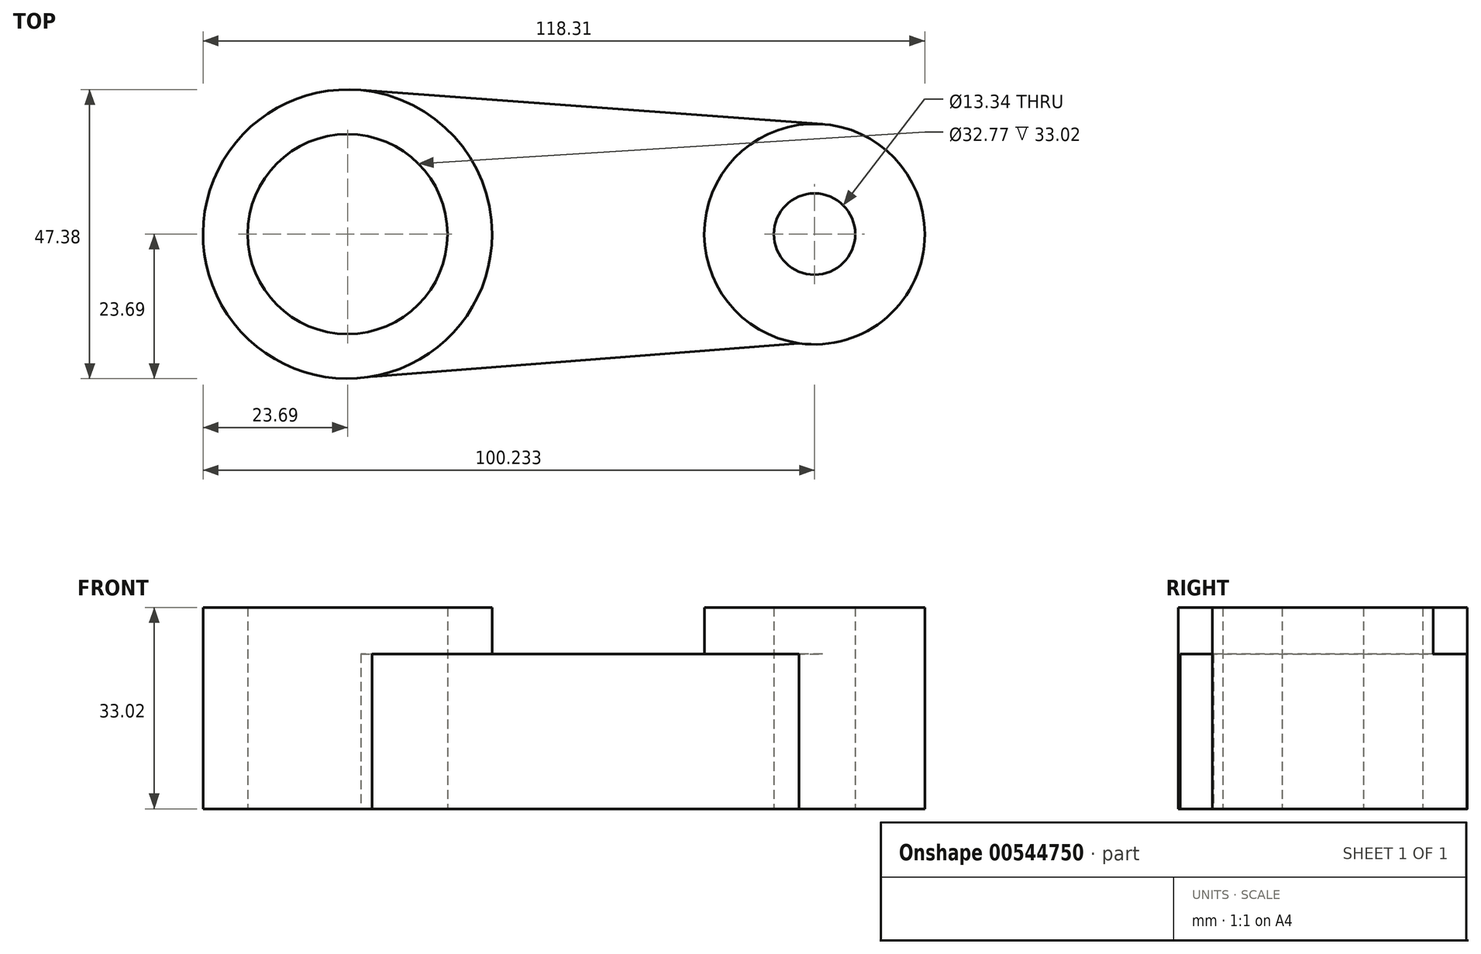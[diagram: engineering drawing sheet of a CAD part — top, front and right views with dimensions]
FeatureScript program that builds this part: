
annotation { "Feature Type Name" : "Feature", "Feature Type Description" : "" }
export const myFeature = defineFeature(function(context is Context, id is Id, definition is map)
    precondition{}
    {
        {
            var Q0;
            Q0=qCreatedBy(makeId("Top.planeOp"),FACE);
            var sketch = newSketch(context, id + "F0", { "sketchPlane" : qUnion([Q0])});
            skCircle(sketch, "E0", {"center": v(0, 0) * mm, "radius": 23.7 * mm});
            skCircle(sketch, "E1", {"center": v(76.54, 0) * mm, "radius": 18.07 * mm});
            skLineSegment(sketch, "E2", {"start": v(2.16, 23.6) * mm, "end": v(77.87, 18.03) * mm});
            skLineSegment(sketch, "E3", {"start": v(4, -23.35) * mm, "end": v(75.29, -17.8) * mm});
            skCircle(sketch, "E4", {"center": v(76.54, 0) * mm, "radius": 6.67 * mm});
            skCircle(sketch, "E5", {"center": v(0, 0) * mm, "radius": 16.38 * mm});
            skSolve(sketch);
        }
        {
            var Q0;
            {var subQ0=sQuery(id+"F0.wireOp",EDGE,"E2");Q0=makeQuery(id+"F0.imprint","IMPRINT",FACE,{"disambiguationData":[TD([[makeQuery(id+"F0.imprint","IMPRINT",EDGE,{"derivedFrom":subQ0}),-1.0]])]});}
            var Q1;
            Q1=makeQuery(id+"F0.imprint","IMPRINT",FACE,{"disambiguationData":[TD([[makeQuery(id+"F0.imprint","IMPRINT",EDGE,{"derivedFrom":sQuery(id+"F0.wireOp",EDGE,"E4")}),-1.0]])]});
            var Q2;
            Q2=makeQuery(id+"F0.imprint","IMPRINT",FACE,{"disambiguationData":[TD([[makeQuery(id+"F0.imprint","IMPRINT",EDGE,{"derivedFrom":sQuery(id+"F0.wireOp",EDGE,"E5")}),-1.0]])]});
            extrude(context, id + "F1", {"entities" : qUnion([Q0, Q1, Q2]), "depth" : 25.4 * mm, "offsetDistance" : 25.4 * mm});
        }
        {
            var Q0;
            Q0=makeQuery(id+"F0.imprint","IMPRINT",FACE,{"disambiguationData":[TD([[makeQuery(id+"F0.imprint","IMPRINT",EDGE,{"derivedFrom":sQuery(id+"F0.wireOp",EDGE,"E5")}),-1.0]])]});
            extrude(context, id + "F2", {"entities" : qUnion([Q0]), "operationType" : NewBodyOperationType.ADD, "depth" : 33.02 * mm, "offsetDistance" : 25.4 * mm});
        }
        {
            var Q0;
            Q0=makeQuery(id+"F0.imprint","IMPRINT",FACE,{"disambiguationData":[TD([[makeQuery(id+"F0.imprint","IMPRINT",EDGE,{"derivedFrom":sQuery(id+"F0.wireOp",EDGE,"E4")}),-1.0]])]});
            extrude(context, id + "F3", {"entities" : qUnion([Q0]), "operationType" : NewBodyOperationType.ADD, "depth" : 33.02 * mm, "offsetDistance" : 25.4 * mm});
        }
    });
